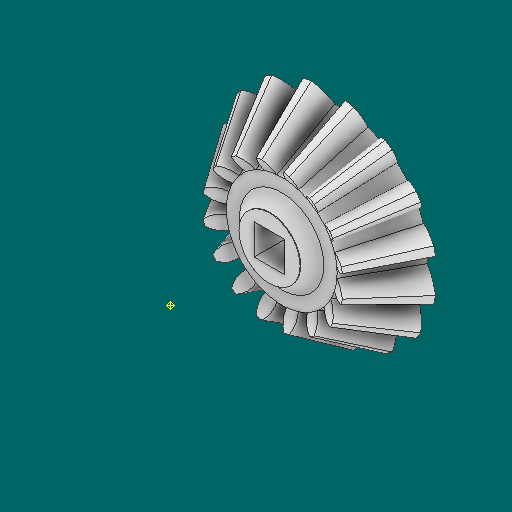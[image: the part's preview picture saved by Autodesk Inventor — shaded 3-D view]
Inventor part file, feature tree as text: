
AUTODESK INVENTOR PART (.ipt)
format: ipt  version: 2023.1 (Build 271208000, 208)  size: 539,136 bytes
history: native  units: mm
features: other x24, loft x2, pattern_circular x2, sketch x2, plane x2, extrude x2, chamfer x1
ambient origin geometry x6: Origin, XZ Plane, X Axis, Y Axis, Z Axis, Center Point
bodies: Solid1 (feature_tree)
feature tree (35):
  other  "Top Point"
  other  "Mesh Plane2"
  other  "Teeth Body"
  other  "Start Point"
  other  "Tooth Plane"
  other  "Start Sketch"
  other  "End Point"
  other  "3D Sketch Right"
  other  "End Plane Right"
  loft  "Loft Right"
  pattern_circular  "Circular Pattern Right"  [2 undecoded]
  other  "3D Sketch Left"
  other  "End Plane Left"
  loft  "Loft Left"
  pattern_circular  "Circular Pattern Left"  Angle=90.0deg  [1 undecoded]
  other  "Fix Body"
  sketch  "Sketch8"  dims[d2=22.50514mm d3=6.985mm d4=16.497551mm d5=90.0deg d7=3.516618mm d8=4.274671mm d9=10.495577mm d11=7.1247mm d12=2.259431mm d15=2.746481mm d16=6.743419mm d17=0.0mm d18=90.0deg d19=0.0mm d20=90.0deg d21=160.0mm d22=360.0deg d26=144.697709mm d27=6.129319mm d28=20.32mm d29=-5.349551mm d30=2.259431mm d31=2.746481mm d32=6.743419mm d35=0.0mm d37=0.0mm d39=0.0mm d40=90.0deg d41=160.0mm d42=360.0deg d46=90.0deg d47=90.0deg d48=0.0mm d49=0.0mm d50=90.0deg d51=1.963495mm d52=0.0mm d53=0.0mm d54=0.0mm d56=6.290752mm d57=13.91815mm d58=9.95067mm d59=8.942426mm d60=6.393316mm d61=8.942426mm d62=6.393316mm d63=90.0deg d64=90.0deg d65=144.697709mm d66=31.5mm d67=20.32mm d68=-5.349551mm d69=6.129319mm d70=2.746481mm d71=6.743419mm d72=2.259431mm d73=6.393316mm d74=8.942426mm d75=0.0mm d76=90.0deg d77=0.0mm d78=90.0deg d79=0.0mm d80=90.0deg d81=160.0mm d82=360.0deg d84=10.0mm d85=20.0mm d86=20.0mm d87=10.0mm d88=0.0mm d89=0.0mm d90=6.35mm d91=3.175mm d92=3.175mm d93=1.27mm d94=0.0mm d95=0.0mm d96=0.0mm d97=1.2mm d98=3.175mm d99=45.0deg]
  plane  "Work Plane6"
  plane  "Work Plane7"
  extrude  "Extrusion1"  Depth=3.175mm
  extrude  "Extrusion2"  Depth=3.175mm
  chamfer  "Chamfer1"  Distance=10.495577mm
  other  "Mesh Plane"
  other  "Top Plane"
  other  "Teeth Body Sketch"
  other  "End Plane"
  other  "End Sketch"
  other  "Helical Curve Left"
  other  "End Sketch Left"
  other  "Body Sketch"
  sketch  "Sketch6"  dims[d0=20.32mm d1=17.697832mm]
  other  "Srf1"
  other  "Helical Curve Right"
  other  "End Sketch Right"
  other  "Pitch Diameter"
note: 3 required parameter values undecoded (feature->parameter linkage not recoverable at this tier; creation-order binding heuristic only, values carry confidence <= 0.55)
